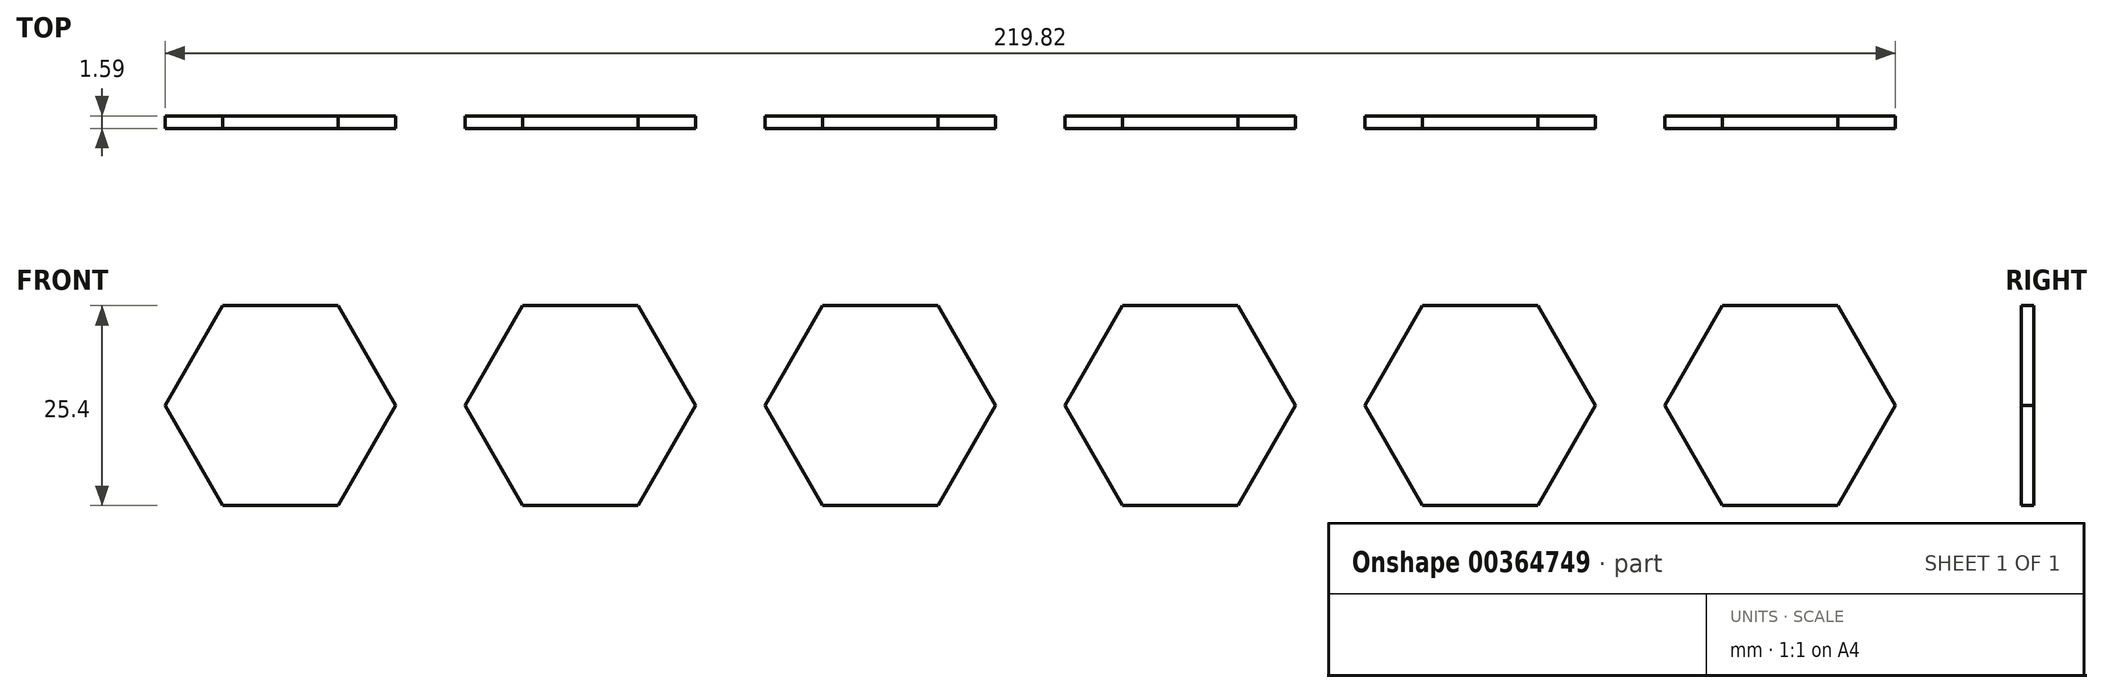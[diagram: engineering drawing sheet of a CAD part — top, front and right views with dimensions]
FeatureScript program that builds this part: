
annotation { "Feature Type Name" : "Feature", "Feature Type Description" : "" }
export const myFeature = defineFeature(function(context is Context, id is Id, definition is map)
    precondition{}
    {
        {
            var Q0;
            Q0=qCreatedBy(makeId("Front.planeOp"),FACE);
            var sketch = newSketch(context, id + "F0", { "sketchPlane" : qUnion([Q0])});
            skCircle(sketch, "E0.cCircle", {"center": v(0, 0) * mm, "radius": 12.7 * mm, "construction": true});
            skLineSegment(sketch, "E0.0", {"start": v(-7.33, 12.7) * mm, "end": v(7.33, 12.7) * mm});
            skLineSegment(sketch, "E0.1", {"start": v(7.33, 12.7) * mm, "end": v(14.66, 0) * mm});
            skLineSegment(sketch, "E0.2", {"start": v(14.66, 0) * mm, "end": v(7.33, -12.7) * mm});
            skLineSegment(sketch, "E0.3", {"start": v(7.33, -12.7) * mm, "end": v(-7.33, -12.7) * mm});
            skLineSegment(sketch, "E0.4", {"start": v(-7.33, -12.7) * mm, "end": v(-14.66, 0) * mm});
            skLineSegment(sketch, "E0.5", {"start": v(-14.66, 0) * mm, "end": v(-7.33, 12.7) * mm});
            skPoint(sketch, "E0.0.midPoint", {"position": v(0, 12.7) * mm});
            skLineSegment(sketch, "E1.1.0.0", {"start": v(45.43, -12.7) * mm, "end": v(30.77, -12.7) * mm});
            skLineSegment(sketch, "E1.1.0.1", {"start": v(52.76, 0) * mm, "end": v(45.43, -12.7) * mm});
            skLineSegment(sketch, "E1.1.0.2", {"start": v(45.43, 12.7) * mm, "end": v(52.76, 0) * mm});
            skLineSegment(sketch, "E1.1.0.3", {"start": v(30.77, 12.7) * mm, "end": v(45.43, 12.7) * mm});
            skLineSegment(sketch, "E1.1.0.4", {"start": v(23.44, 0) * mm, "end": v(30.77, 12.7) * mm});
            skLineSegment(sketch, "E1.1.0.5", {"start": v(30.77, -12.7) * mm, "end": v(23.44, 0) * mm});
            skLineSegment(sketch, "E1.2.0.0", {"start": v(83.53, -12.7) * mm, "end": v(68.87, -12.7) * mm});
            skLineSegment(sketch, "E1.2.0.1", {"start": v(90.86, 0) * mm, "end": v(83.53, -12.7) * mm});
            skLineSegment(sketch, "E1.2.0.2", {"start": v(83.53, 12.7) * mm, "end": v(90.86, 0) * mm});
            skLineSegment(sketch, "E1.2.0.3", {"start": v(68.87, 12.7) * mm, "end": v(83.53, 12.7) * mm});
            skLineSegment(sketch, "E1.2.0.4", {"start": v(61.54, 0) * mm, "end": v(68.87, 12.7) * mm});
            skLineSegment(sketch, "E1.2.0.5", {"start": v(68.87, -12.7) * mm, "end": v(61.54, 0) * mm});
            skLineSegment(sketch, "E1.3.0.0", {"start": v(121.63, -12.7) * mm, "end": v(106.97, -12.7) * mm});
            skLineSegment(sketch, "E1.3.0.1", {"start": v(128.96, 0) * mm, "end": v(121.63, -12.7) * mm});
            skLineSegment(sketch, "E1.3.0.2", {"start": v(121.63, 12.7) * mm, "end": v(128.96, 0) * mm});
            skLineSegment(sketch, "E1.3.0.3", {"start": v(106.97, 12.7) * mm, "end": v(121.63, 12.7) * mm});
            skLineSegment(sketch, "E1.3.0.4", {"start": v(99.64, 0) * mm, "end": v(106.97, 12.7) * mm});
            skLineSegment(sketch, "E1.3.0.5", {"start": v(106.97, -12.7) * mm, "end": v(99.64, 0) * mm});
            skLineSegment(sketch, "E1.4.0.0", {"start": v(159.73, -12.7) * mm, "end": v(145.07, -12.7) * mm});
            skLineSegment(sketch, "E1.4.0.1", {"start": v(167.06, 0) * mm, "end": v(159.73, -12.7) * mm});
            skLineSegment(sketch, "E1.4.0.2", {"start": v(159.73, 12.7) * mm, "end": v(167.06, 0) * mm});
            skLineSegment(sketch, "E1.4.0.3", {"start": v(145.07, 12.7) * mm, "end": v(159.73, 12.7) * mm});
            skLineSegment(sketch, "E1.4.0.4", {"start": v(137.74, 0) * mm, "end": v(145.07, 12.7) * mm});
            skLineSegment(sketch, "E1.4.0.5", {"start": v(145.07, -12.7) * mm, "end": v(137.74, 0) * mm});
            skLineSegment(sketch, "E1.5.0.0", {"start": v(197.83, -12.7) * mm, "end": v(183.17, -12.7) * mm});
            skLineSegment(sketch, "E1.5.0.1", {"start": v(205.16, 0) * mm, "end": v(197.83, -12.7) * mm});
            skLineSegment(sketch, "E1.5.0.2", {"start": v(197.83, 12.7) * mm, "end": v(205.16, 0) * mm});
            skLineSegment(sketch, "E1.5.0.3", {"start": v(183.17, 12.7) * mm, "end": v(197.83, 12.7) * mm});
            skLineSegment(sketch, "E1.5.0.4", {"start": v(175.84, 0) * mm, "end": v(183.17, 12.7) * mm});
            skLineSegment(sketch, "E1.5.0.5", {"start": v(183.17, -12.7) * mm, "end": v(175.84, 0) * mm});
            skLineSegment(sketch, "E1.direction1", {"start": v(-7.33, -12.7) * mm, "end": v(30.77, -12.7) * mm, "construction": true});
            skLineSegment(sketch, "E2.0.1.0", {"start": v(45.43, 25.15) * mm, "end": v(30.77, 25.15) * mm});
            skLineSegment(sketch, "E2.0.1.1", {"start": v(52.76, 37.85) * mm, "end": v(45.43, 25.15) * mm});
            skLineSegment(sketch, "E2.0.1.2", {"start": v(45.43, 50.55) * mm, "end": v(52.76, 37.85) * mm});
            skLineSegment(sketch, "E2.0.1.3", {"start": v(30.77, 50.55) * mm, "end": v(45.43, 50.55) * mm});
            skLineSegment(sketch, "E2.0.1.4", {"start": v(23.44, 37.85) * mm, "end": v(30.77, 50.55) * mm});
            skLineSegment(sketch, "E2.0.1.5", {"start": v(159.73, 50.55) * mm, "end": v(167.06, 37.85) * mm});
            skLineSegment(sketch, "E2.0.1.6", {"start": v(30.77, 25.15) * mm, "end": v(23.44, 37.85) * mm});
            skLineSegment(sketch, "E2.0.1.7", {"start": v(99.64, 37.85) * mm, "end": v(106.97, 50.55) * mm});
            skLineSegment(sketch, "E2.0.1.8", {"start": v(-7.33, 25.15) * mm, "end": v(-14.66, 37.85) * mm});
            skCircle(sketch, "E2.0.1.9", {"center": v(0, 37.85) * mm, "radius": 12.7 * mm, "construction": true});
            skLineSegment(sketch, "E2.0.1.10", {"start": v(83.53, 50.55) * mm, "end": v(90.86, 37.85) * mm});
            skLineSegment(sketch, "E2.0.1.11", {"start": v(90.86, 37.85) * mm, "end": v(83.53, 25.15) * mm});
            skLineSegment(sketch, "E2.0.1.12", {"start": v(83.53, 25.15) * mm, "end": v(68.87, 25.15) * mm});
            skLineSegment(sketch, "E2.0.1.13", {"start": v(175.84, 37.85) * mm, "end": v(183.17, 50.55) * mm});
            skLineSegment(sketch, "E2.0.1.14", {"start": v(121.63, 25.15) * mm, "end": v(106.97, 25.15) * mm});
            skLineSegment(sketch, "E2.0.1.15", {"start": v(167.06, 37.85) * mm, "end": v(159.73, 25.15) * mm});
            skLineSegment(sketch, "E2.0.1.16", {"start": v(128.96, 37.85) * mm, "end": v(121.63, 25.15) * mm});
            skPoint(sketch, "E2.0.1.17", {"position": v(0, 50.55) * mm});
            skLineSegment(sketch, "E2.0.1.18", {"start": v(183.17, 25.15) * mm, "end": v(175.84, 37.85) * mm});
            skLineSegment(sketch, "E2.0.1.19", {"start": v(137.74, 37.85) * mm, "end": v(145.07, 50.55) * mm});
            skLineSegment(sketch, "E2.0.1.20", {"start": v(68.87, 50.55) * mm, "end": v(83.53, 50.55) * mm});
            skLineSegment(sketch, "E2.0.1.21", {"start": v(205.16, 37.85) * mm, "end": v(197.83, 25.15) * mm});
            skLineSegment(sketch, "E2.0.1.22", {"start": v(145.07, 50.55) * mm, "end": v(159.73, 50.55) * mm});
            skLineSegment(sketch, "E2.0.1.23", {"start": v(106.97, 25.15) * mm, "end": v(99.64, 37.85) * mm});
            skLineSegment(sketch, "E2.0.1.24", {"start": v(121.63, 50.55) * mm, "end": v(128.96, 37.85) * mm});
            skLineSegment(sketch, "E2.0.1.25", {"start": v(145.07, 25.15) * mm, "end": v(137.74, 37.85) * mm});
            skLineSegment(sketch, "E2.0.1.26", {"start": v(-7.33, 25.15) * mm, "end": v(30.77, 25.15) * mm, "construction": true});
            skLineSegment(sketch, "E2.0.1.27", {"start": v(61.54, 37.85) * mm, "end": v(68.87, 50.55) * mm});
            skLineSegment(sketch, "E2.0.1.28", {"start": v(197.83, 50.55) * mm, "end": v(205.16, 37.85) * mm});
            skLineSegment(sketch, "E2.0.1.29", {"start": v(159.73, 25.15) * mm, "end": v(145.07, 25.15) * mm});
            skLineSegment(sketch, "E2.0.1.30", {"start": v(106.97, 50.55) * mm, "end": v(121.63, 50.55) * mm});
            skLineSegment(sketch, "E2.0.1.31", {"start": v(197.83, 25.15) * mm, "end": v(183.17, 25.15) * mm});
            skLineSegment(sketch, "E2.0.1.32", {"start": v(68.87, 25.15) * mm, "end": v(61.54, 37.85) * mm});
            skLineSegment(sketch, "E2.0.1.33", {"start": v(183.17, 50.55) * mm, "end": v(197.83, 50.55) * mm});
            skLineSegment(sketch, "E2.0.1.34", {"start": v(7.33, 50.55) * mm, "end": v(14.66, 37.85) * mm});
            skLineSegment(sketch, "E2.0.1.35", {"start": v(14.66, 37.85) * mm, "end": v(7.33, 25.15) * mm});
            skLineSegment(sketch, "E2.0.1.36", {"start": v(-14.66, 37.85) * mm, "end": v(-7.33, 50.55) * mm});
            skLineSegment(sketch, "E2.0.1.37", {"start": v(7.33, 25.15) * mm, "end": v(-7.33, 25.15) * mm});
            skLineSegment(sketch, "E2.0.1.38", {"start": v(-7.33, 50.55) * mm, "end": v(7.33, 50.55) * mm});
            skLineSegment(sketch, "E2.1.1.0", {"start": v(45.43, 25.15) * mm, "end": v(30.77, 25.15) * mm});
            skLineSegment(sketch, "E2.1.1.1", {"start": v(52.76, 37.85) * mm, "end": v(45.43, 25.15) * mm});
            skLineSegment(sketch, "E2.1.1.2", {"start": v(45.43, 50.55) * mm, "end": v(52.76, 37.85) * mm});
            skLineSegment(sketch, "E2.1.1.3", {"start": v(30.77, 50.55) * mm, "end": v(45.43, 50.55) * mm});
            skLineSegment(sketch, "E2.1.1.4", {"start": v(23.44, 37.85) * mm, "end": v(30.77, 50.55) * mm});
            skLineSegment(sketch, "E2.1.1.5", {"start": v(159.73, 50.55) * mm, "end": v(167.06, 37.85) * mm});
            skLineSegment(sketch, "E2.1.1.6", {"start": v(30.77, 25.15) * mm, "end": v(23.44, 37.85) * mm});
            skLineSegment(sketch, "E2.1.1.7", {"start": v(99.64, 37.85) * mm, "end": v(106.97, 50.55) * mm});
            skLineSegment(sketch, "E2.1.1.8", {"start": v(-7.33, 25.15) * mm, "end": v(-14.66, 37.85) * mm});
            skCircle(sketch, "E2.1.1.9", {"center": v(0, 37.85) * mm, "radius": 12.7 * mm, "construction": true});
            skLineSegment(sketch, "E2.1.1.10", {"start": v(83.53, 50.55) * mm, "end": v(90.86, 37.85) * mm});
            skLineSegment(sketch, "E2.1.1.11", {"start": v(90.86, 37.85) * mm, "end": v(83.53, 25.15) * mm});
            skLineSegment(sketch, "E2.1.1.12", {"start": v(83.53, 25.15) * mm, "end": v(68.87, 25.15) * mm});
            skLineSegment(sketch, "E2.1.1.13", {"start": v(175.84, 37.85) * mm, "end": v(183.17, 50.55) * mm});
            skLineSegment(sketch, "E2.1.1.14", {"start": v(121.63, 25.15) * mm, "end": v(106.97, 25.15) * mm});
            skLineSegment(sketch, "E2.1.1.15", {"start": v(167.06, 37.85) * mm, "end": v(159.73, 25.15) * mm});
            skLineSegment(sketch, "E2.1.1.16", {"start": v(128.96, 37.85) * mm, "end": v(121.63, 25.15) * mm});
            skPoint(sketch, "E2.1.1.17", {"position": v(0, 50.55) * mm});
            skLineSegment(sketch, "E2.1.1.18", {"start": v(183.17, 25.15) * mm, "end": v(175.84, 37.85) * mm});
            skLineSegment(sketch, "E2.1.1.19", {"start": v(137.74, 37.85) * mm, "end": v(145.07, 50.55) * mm});
            skLineSegment(sketch, "E2.1.1.20", {"start": v(68.87, 50.55) * mm, "end": v(83.53, 50.55) * mm});
            skLineSegment(sketch, "E2.1.1.21", {"start": v(205.16, 37.85) * mm, "end": v(197.83, 25.15) * mm});
            skLineSegment(sketch, "E2.1.1.22", {"start": v(145.07, 50.55) * mm, "end": v(159.73, 50.55) * mm});
            skLineSegment(sketch, "E2.1.1.23", {"start": v(106.97, 25.15) * mm, "end": v(99.64, 37.85) * mm});
            skLineSegment(sketch, "E2.1.1.24", {"start": v(121.63, 50.55) * mm, "end": v(128.96, 37.85) * mm});
            skLineSegment(sketch, "E2.1.1.25", {"start": v(145.07, 25.15) * mm, "end": v(137.74, 37.85) * mm});
            skLineSegment(sketch, "E2.1.1.26", {"start": v(-7.33, 25.15) * mm, "end": v(30.77, 25.15) * mm, "construction": true});
            skLineSegment(sketch, "E2.1.1.27", {"start": v(61.54, 37.85) * mm, "end": v(68.87, 50.55) * mm});
            skLineSegment(sketch, "E2.1.1.28", {"start": v(197.83, 50.55) * mm, "end": v(205.16, 37.85) * mm});
            skLineSegment(sketch, "E2.1.1.29", {"start": v(159.73, 25.15) * mm, "end": v(145.07, 25.15) * mm});
            skLineSegment(sketch, "E2.1.1.30", {"start": v(106.97, 50.55) * mm, "end": v(121.63, 50.55) * mm});
            skLineSegment(sketch, "E2.1.1.31", {"start": v(197.83, 25.15) * mm, "end": v(183.17, 25.15) * mm});
            skLineSegment(sketch, "E2.1.1.32", {"start": v(68.87, 25.15) * mm, "end": v(61.54, 37.85) * mm});
            skLineSegment(sketch, "E2.1.1.33", {"start": v(183.17, 50.55) * mm, "end": v(197.83, 50.55) * mm});
            skLineSegment(sketch, "E2.1.1.34", {"start": v(7.33, 50.55) * mm, "end": v(14.66, 37.85) * mm});
            skLineSegment(sketch, "E2.1.1.35", {"start": v(14.66, 37.85) * mm, "end": v(7.33, 25.15) * mm});
            skLineSegment(sketch, "E2.1.1.36", {"start": v(-14.66, 37.85) * mm, "end": v(-7.33, 50.55) * mm});
            skLineSegment(sketch, "E2.1.1.37", {"start": v(7.33, 25.15) * mm, "end": v(-7.33, 25.15) * mm});
            skLineSegment(sketch, "E2.1.1.38", {"start": v(-7.33, 50.55) * mm, "end": v(7.33, 50.55) * mm});
            skLineSegment(sketch, "E2.2.1.0", {"start": v(45.43, 25.15) * mm, "end": v(30.77, 25.15) * mm});
            skLineSegment(sketch, "E2.2.1.1", {"start": v(52.76, 37.85) * mm, "end": v(45.43, 25.15) * mm});
            skLineSegment(sketch, "E2.2.1.2", {"start": v(45.43, 50.55) * mm, "end": v(52.76, 37.85) * mm});
            skLineSegment(sketch, "E2.2.1.3", {"start": v(30.77, 50.55) * mm, "end": v(45.43, 50.55) * mm});
            skLineSegment(sketch, "E2.2.1.4", {"start": v(23.44, 37.85) * mm, "end": v(30.77, 50.55) * mm});
            skLineSegment(sketch, "E2.2.1.5", {"start": v(159.73, 50.55) * mm, "end": v(167.06, 37.85) * mm});
            skLineSegment(sketch, "E2.2.1.6", {"start": v(30.77, 25.15) * mm, "end": v(23.44, 37.85) * mm});
            skLineSegment(sketch, "E2.2.1.7", {"start": v(99.64, 37.85) * mm, "end": v(106.97, 50.55) * mm});
            skLineSegment(sketch, "E2.2.1.8", {"start": v(-7.33, 25.15) * mm, "end": v(-14.66, 37.85) * mm});
            skCircle(sketch, "E2.2.1.9", {"center": v(0, 37.85) * mm, "radius": 12.7 * mm, "construction": true});
            skLineSegment(sketch, "E2.2.1.10", {"start": v(83.53, 50.55) * mm, "end": v(90.86, 37.85) * mm});
            skLineSegment(sketch, "E2.2.1.11", {"start": v(90.86, 37.85) * mm, "end": v(83.53, 25.15) * mm});
            skLineSegment(sketch, "E2.2.1.12", {"start": v(83.53, 25.15) * mm, "end": v(68.87, 25.15) * mm});
            skLineSegment(sketch, "E2.2.1.13", {"start": v(175.84, 37.85) * mm, "end": v(183.17, 50.55) * mm});
            skLineSegment(sketch, "E2.2.1.14", {"start": v(121.63, 25.15) * mm, "end": v(106.97, 25.15) * mm});
            skLineSegment(sketch, "E2.2.1.15", {"start": v(167.06, 37.85) * mm, "end": v(159.73, 25.15) * mm});
            skLineSegment(sketch, "E2.2.1.16", {"start": v(128.96, 37.85) * mm, "end": v(121.63, 25.15) * mm});
            skPoint(sketch, "E2.2.1.17", {"position": v(0, 50.55) * mm});
            skLineSegment(sketch, "E2.2.1.18", {"start": v(183.17, 25.15) * mm, "end": v(175.84, 37.85) * mm});
            skLineSegment(sketch, "E2.2.1.19", {"start": v(137.74, 37.85) * mm, "end": v(145.07, 50.55) * mm});
            skLineSegment(sketch, "E2.2.1.20", {"start": v(68.87, 50.55) * mm, "end": v(83.53, 50.55) * mm});
            skLineSegment(sketch, "E2.2.1.21", {"start": v(205.16, 37.85) * mm, "end": v(197.83, 25.15) * mm});
            skLineSegment(sketch, "E2.2.1.22", {"start": v(145.07, 50.55) * mm, "end": v(159.73, 50.55) * mm});
            skLineSegment(sketch, "E2.2.1.23", {"start": v(106.97, 25.15) * mm, "end": v(99.64, 37.85) * mm});
            skLineSegment(sketch, "E2.2.1.24", {"start": v(121.63, 50.55) * mm, "end": v(128.96, 37.85) * mm});
            skLineSegment(sketch, "E2.2.1.25", {"start": v(145.07, 25.15) * mm, "end": v(137.74, 37.85) * mm});
            skLineSegment(sketch, "E2.2.1.26", {"start": v(-7.33, 25.15) * mm, "end": v(30.77, 25.15) * mm, "construction": true});
            skLineSegment(sketch, "E2.2.1.27", {"start": v(61.54, 37.85) * mm, "end": v(68.87, 50.55) * mm});
            skLineSegment(sketch, "E2.2.1.28", {"start": v(197.83, 50.55) * mm, "end": v(205.16, 37.85) * mm});
            skLineSegment(sketch, "E2.2.1.29", {"start": v(159.73, 25.15) * mm, "end": v(145.07, 25.15) * mm});
            skLineSegment(sketch, "E2.2.1.30", {"start": v(106.97, 50.55) * mm, "end": v(121.63, 50.55) * mm});
            skLineSegment(sketch, "E2.2.1.31", {"start": v(197.83, 25.15) * mm, "end": v(183.17, 25.15) * mm});
            skLineSegment(sketch, "E2.2.1.32", {"start": v(68.87, 25.15) * mm, "end": v(61.54, 37.85) * mm});
            skLineSegment(sketch, "E2.2.1.33", {"start": v(183.17, 50.55) * mm, "end": v(197.83, 50.55) * mm});
            skLineSegment(sketch, "E2.2.1.34", {"start": v(7.33, 50.55) * mm, "end": v(14.66, 37.85) * mm});
            skLineSegment(sketch, "E2.2.1.35", {"start": v(14.66, 37.85) * mm, "end": v(7.33, 25.15) * mm});
            skLineSegment(sketch, "E2.2.1.36", {"start": v(-14.66, 37.85) * mm, "end": v(-7.33, 50.55) * mm});
            skLineSegment(sketch, "E2.2.1.37", {"start": v(7.33, 25.15) * mm, "end": v(-7.33, 25.15) * mm});
            skLineSegment(sketch, "E2.2.1.38", {"start": v(-7.33, 50.55) * mm, "end": v(7.33, 50.55) * mm});
            skLineSegment(sketch, "E2.direction1", {"start": v(-7.33, -12.7) * mm, "end": v(-7.33, -12.7) * mm});
            skLineSegment(sketch, "E2.direction2", {"start": v(-7.33, -12.7) * mm, "end": v(-7.33, 25.15) * mm, "construction": true});
            skSolve(sketch);
        }
        {
            var Q0;
            Q0=makeQuery(id+"F0.imprint","IMPRINT",FACE,{"disambiguationData":[TD([[makeQuery(id+"F0.imprint","IMPRINT",EDGE,{"derivedFrom":sQuery(id+"F0.wireOp",EDGE,"E0.4")}),-1.0]])]});
            var Q1;
            Q1=makeQuery(id+"F0.imprint","IMPRINT",FACE,{"disambiguationData":[TD([[makeQuery(id+"F0.imprint","IMPRINT",EDGE,{"derivedFrom":sQuery(id+"F0.wireOp",EDGE,"E1.1.0.0")}),-1.0]])]});
            var Q2;
            Q2=makeQuery(id+"F0.imprint","IMPRINT",FACE,{"disambiguationData":[TD([[makeQuery(id+"F0.imprint","IMPRINT",EDGE,{"derivedFrom":sQuery(id+"F0.wireOp",EDGE,"E1.2.0.2")}),-1.0]])]});
            var Q3;
            Q3=makeQuery(id+"F0.imprint","IMPRINT",FACE,{"disambiguationData":[TD([[makeQuery(id+"F0.imprint","IMPRINT",EDGE,{"derivedFrom":sQuery(id+"F0.wireOp",EDGE,"E1.3.0.4")}),-1.0]])]});
            var Q4;
            Q4=makeQuery(id+"F0.imprint","IMPRINT",FACE,{"disambiguationData":[TD([[makeQuery(id+"F0.imprint","IMPRINT",EDGE,{"derivedFrom":sQuery(id+"F0.wireOp",EDGE,"E1.4.0.2")}),-1.0]])]});
            var Q5;
            Q5=makeQuery(id+"F0.imprint","IMPRINT",FACE,{"disambiguationData":[TD([[makeQuery(id+"F0.imprint","IMPRINT",EDGE,{"derivedFrom":sQuery(id+"F0.wireOp",EDGE,"E1.5.0.4")}),-1.0]])]});
            var Q6;
            Q6=makeQuery(id+"F0.imprint","IMPRINT",FACE,{"disambiguationData":[TD([[makeQuery(id+"F0.imprint","IMPRINT",EDGE,{"derivedFrom":sQuery(id+"F0.wireOp",EDGE,"E2.2.1.13")}),-1.0]])]});
            var Q7;
            Q7=makeQuery(id+"F0.imprint","IMPRINT",FACE,{"disambiguationData":[TD([[makeQuery(id+"F0.imprint","IMPRINT",EDGE,{"derivedFrom":sQuery(id+"F0.wireOp",EDGE,"E2.2.1.5")}),-1.0]])]});
            var Q8;
            Q8=makeQuery(id+"F0.imprint","IMPRINT",FACE,{"disambiguationData":[TD([[makeQuery(id+"F0.imprint","IMPRINT",EDGE,{"derivedFrom":sQuery(id+"F0.wireOp",EDGE,"E2.2.1.7")}),-1.0]])]});
            var Q9;
            Q9=makeQuery(id+"F0.imprint","IMPRINT",FACE,{"disambiguationData":[TD([[makeQuery(id+"F0.imprint","IMPRINT",EDGE,{"derivedFrom":sQuery(id+"F0.wireOp",EDGE,"E2.2.1.10")}),-1.0]])]});
            var Q10;
            Q10=makeQuery(id+"F0.imprint","IMPRINT",FACE,{"disambiguationData":[TD([[makeQuery(id+"F0.imprint","IMPRINT",EDGE,{"derivedFrom":sQuery(id+"F0.wireOp",EDGE,"E2.2.1.0")}),-1.0]])]});
            var Q11;
            Q11=makeQuery(id+"F0.imprint","IMPRINT",FACE,{"disambiguationData":[TD([[makeQuery(id+"F0.imprint","IMPRINT",EDGE,{"derivedFrom":sQuery(id+"F0.wireOp",EDGE,"E2.2.1.8")}),-1.0]])]});
            extrude(context, id + "F1", {"entities" : qUnion([Q0, Q1, Q2, Q3, Q4, Q5, Q6, Q7, Q8, Q9, Q10, Q11]), "depth" : 1.59 * mm});
        }
    });
